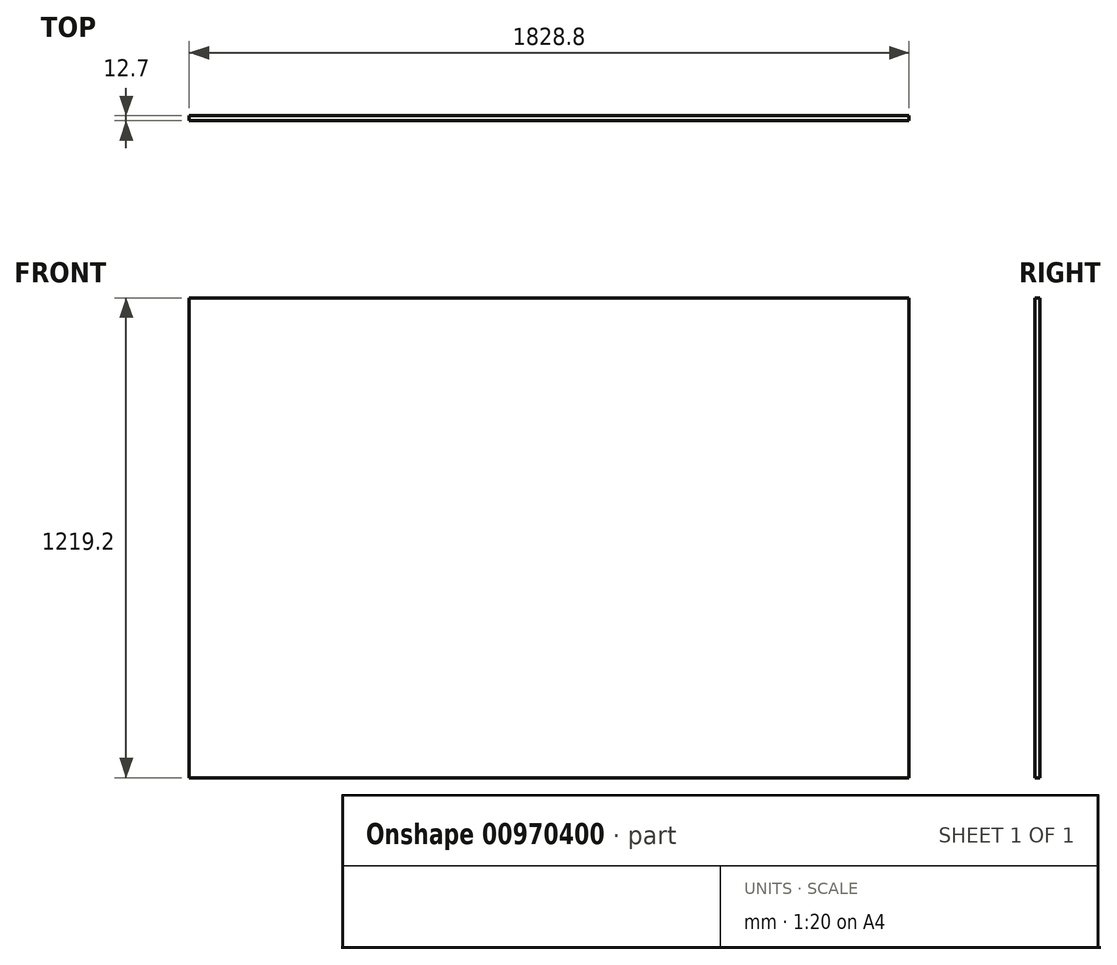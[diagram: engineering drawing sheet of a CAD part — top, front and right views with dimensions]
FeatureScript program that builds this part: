
annotation { "Feature Type Name" : "Feature", "Feature Type Description" : "" }
export const myFeature = defineFeature(function(context is Context, id is Id, definition is map)
    precondition{}
    {
        {
            var Q0;
            Q0=qCreatedBy(makeId("Front.planeOp"),FACE);
            var sketch = newSketch(context, id + "F0", { "sketchPlane" : qUnion([Q0])});
            skLineSegment(sketch, "E0.bottom", {"start": v(0, 0) * mm, "end": v(1828.8, 0) * mm});
            skLineSegment(sketch, "E0.top", {"start": v(0, -1219.2) * mm, "end": v(1828.8, -1219.2) * mm});
            skLineSegment(sketch, "E0.left", {"start": v(0, 0) * mm, "end": v(0, -1219.2) * mm});
            skLineSegment(sketch, "E0.right", {"start": v(1828.8, 0) * mm, "end": v(1828.8, -1219.2) * mm});
            skSolve(sketch);
        }
        {
            var Q0;
            Q0=makeQuery(id+"F0.imprint","IMPRINT",FACE,{"disambiguationData":[TD([[makeQuery(id+"F0.imprint","IMPRINT",EDGE,{"derivedFrom":sQuery(id+"F0.wireOp",EDGE,"E0.bottom")}),-1.0]])]});
            extrude(context, id + "F1", {"entities" : qUnion([Q0]), "depth" : 12.7 * mm, "offsetDistance" : 25.4 * mm});
        }
    });
